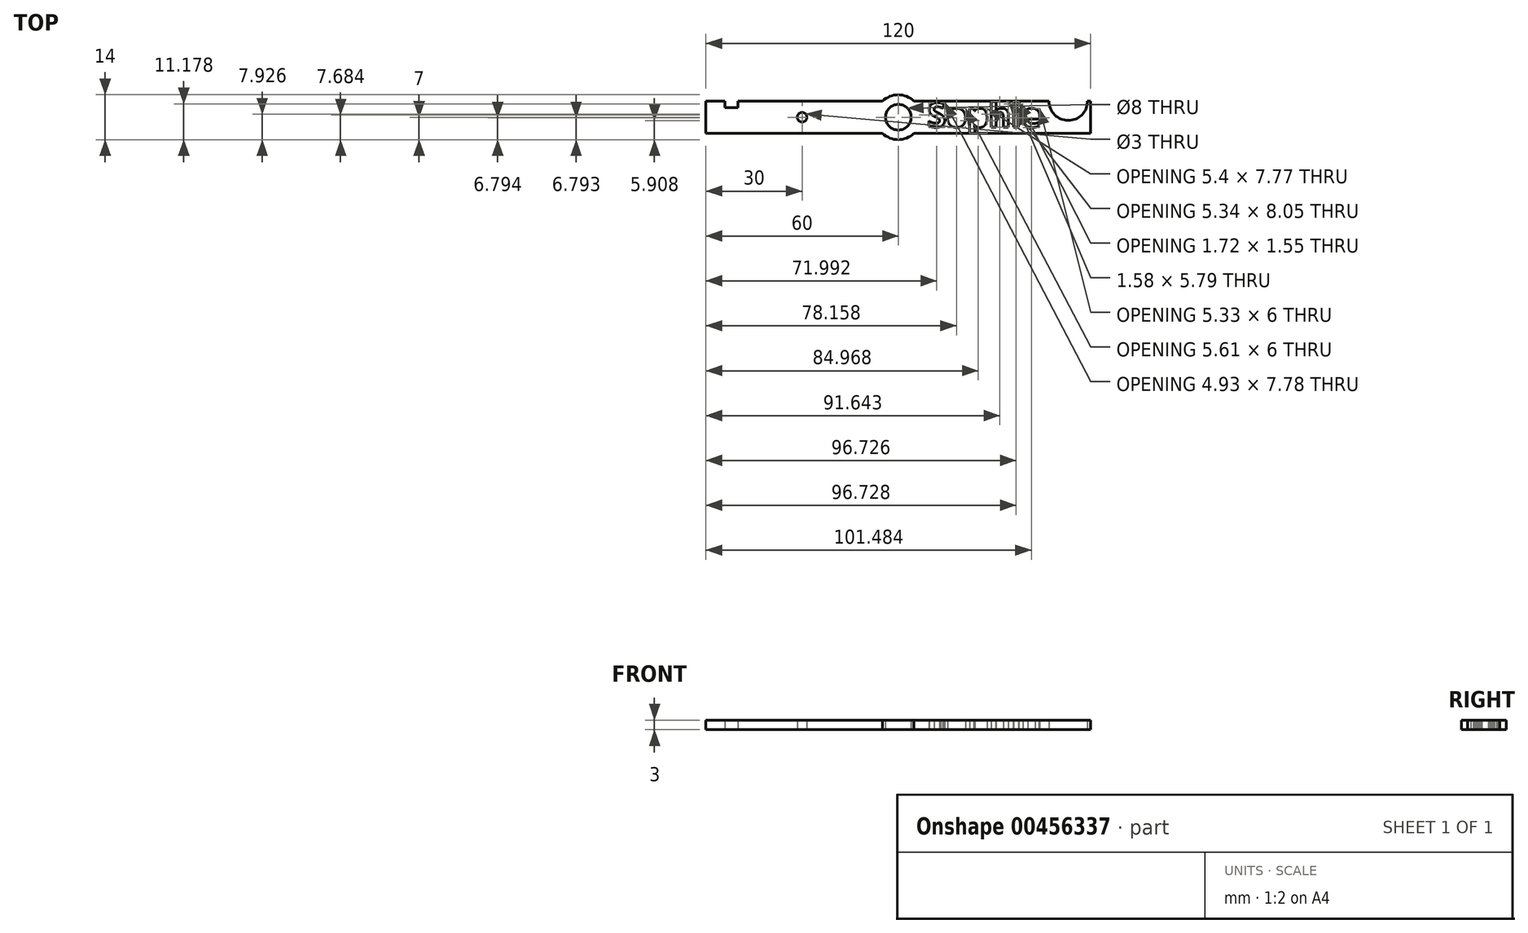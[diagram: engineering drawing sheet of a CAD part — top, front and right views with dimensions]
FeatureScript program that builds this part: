
annotation { "Feature Type Name" : "Feature", "Feature Type Description" : "" }
export const myFeature = defineFeature(function(context is Context, id is Id, definition is map)
    precondition{}
    {
        {
            var Q0;
            Q0=qCreatedBy(makeId("Top.planeOp"),FACE);
            var sketch = newSketch(context, id + "F0", { "sketchPlane" : qUnion([Q0])});
            skLineSegment(sketch, "E0.bottom", {"start": v(-60, 5) * mm, "end": v(60, 5) * mm});
            skLineSegment(sketch, "E0.top", {"start": v(-60, -5) * mm, "end": v(60, -5) * mm});
            skLineSegment(sketch, "E0.left", {"start": v(-60, 5) * mm, "end": v(-60, -5) * mm});
            skLineSegment(sketch, "E0.right", {"start": v(60, 5) * mm, "end": v(60, -5) * mm});
            skPoint(sketch, "E0.middle", {"position": v(0, 0) * mm});
            skLineSegment(sketch, "E1.bottom", {"start": v(-54.04, 5) * mm, "end": v(-50.04, 5) * mm});
            skLineSegment(sketch, "E1.top", {"start": v(-54.04, 3) * mm, "end": v(-50.04, 3) * mm});
            skLineSegment(sketch, "E1.left", {"start": v(-54.04, 5) * mm, "end": v(-54.04, 3) * mm});
            skLineSegment(sketch, "E1.right", {"start": v(-50.04, 5) * mm, "end": v(-50.04, 3) * mm});
            skCircle(sketch, "E2", {"center": v(0, 0) * mm, "radius": 4 * mm});
            skCircle(sketch, "E3", {"center": v(0, 0) * mm, "radius": 7 * mm});
            skCircle(sketch, "E4", {"center": v(-30, 0) * mm, "radius": 1.5 * mm});
            skPoint(sketch, "E4.second.point", {"position": v(-31.27, 0.8) * mm});
            skPoint(sketch, "E4.third.point", {"position": v(-31.07, -1.06) * mm});
            skCircle(sketch, "E5", {"center": v(53, 5) * mm, "radius": 6 * mm});
            skText(sketch, "E6", { "text": "Sophie\n", "fontName": "OpenSans-Bold.ttf"});
            skLineSegment(sketch, "E7", {"start": v(21.79, -4.98) * mm, "end": v(24.54, -4.98) * mm});
            const initialGuessF0  = {"E6": [0.00904, -0.0031, 1, 0, 0.00763]};
            skSetInitialGuess(sketch, initialGuessF0);
            skSolve(sketch);
        }
        {
            var Q0;
            {var subQ0=sQuery(id+"F0.wireOp",EDGE,"E0.left");Q0=makeQuery(id+"F0.imprint","IMPRINT",FACE,{"disambiguationData":[TD([[makeQuery(id+"F0.imprint","IMPRINT",EDGE,{"derivedFrom":subQ0}),1.0]])]});}
            var Q1;
            Q1=makeQuery(id+"F0.imprint","IMPRINT",FACE,{"disambiguationData":[TD([[makeQuery(id+"F0.imprint","IMPRINT",EDGE,{"derivedFrom":sQuery(id+"F0.wireOp",EDGE,"E2")}),-1.0]])]});
            var Q2;
            {var subQ0=sQuery(id+"F0.wireOp",EDGE,"E3");var subQ1=sQuery(id+"F0.wireOp",EDGE,"E0.top");var subQ2=makeQuery(id+"F0.imprint","INTERSECT",VERTEX,{"disambiguationData":[OD(0.0)],"derivedFrom":[subQ1,subQ0]});Q2=makeQuery(id+"F0.imprint","IMPRINT",FACE,{"disambiguationData":[TD([[makeQuery(id+"F0.imprint","IMPRINT",EDGE,{"disambiguationData":[TD([[subQ2,-1.0]])],"derivedFrom":subQ1}),-1.0]])]});}
            var Q3;
            {var subQ0=sQuery(id+"F0.wireOp",EDGE,"E3");var subQ1=sQuery(id+"F0.wireOp",EDGE,"E0.bottom");var subQ2=makeQuery(id+"F0.imprint","INTERSECT",VERTEX,{"disambiguationData":[OD(0.0)],"derivedFrom":[subQ1,subQ0]});Q3=makeQuery(id+"F0.imprint","IMPRINT",FACE,{"disambiguationData":[TD([[makeQuery(id+"F0.imprint","IMPRINT",EDGE,{"disambiguationData":[TD([[subQ2,-1.0]])],"derivedFrom":subQ1}),1.0]])]});}
            var Q4;
            {var subQ0=sQuery(id+"F0.wireOp",EDGE,"E0.right");Q4=makeQuery(id+"F0.imprint","IMPRINT",FACE,{"disambiguationData":[TD([[makeQuery(id+"F0.imprint","IMPRINT",EDGE,{"derivedFrom":subQ0}),-1.0]])]});}
            var Q5;
            {var subQ0=sQuery(id+"F0.wireOp",EDGE,"E6.sketch_text.stroke-51");var subQ1=sQuery(id+"F0.wireOp",EDGE,"E0.top");var subQ2=makeQuery(id+"F0.imprint","INTERSECT",VERTEX,{"derivedFrom":[subQ1,subQ0]});Q5=makeQuery(id+"F0.imprint","IMPRINT",FACE,{"disambiguationData":[TD([[makeQuery(id+"F0.imprint","IMPRINT",EDGE,{"disambiguationData":[TD([[subQ2,-1.0]])],"derivedFrom":subQ1}),1.0]])]});}
            extrude(context, id + "F1", {"entities" : qUnion([Q0, Q1, Q2, Q3, Q4, Q5]), "depth" : 3 * mm});
        }
    });
